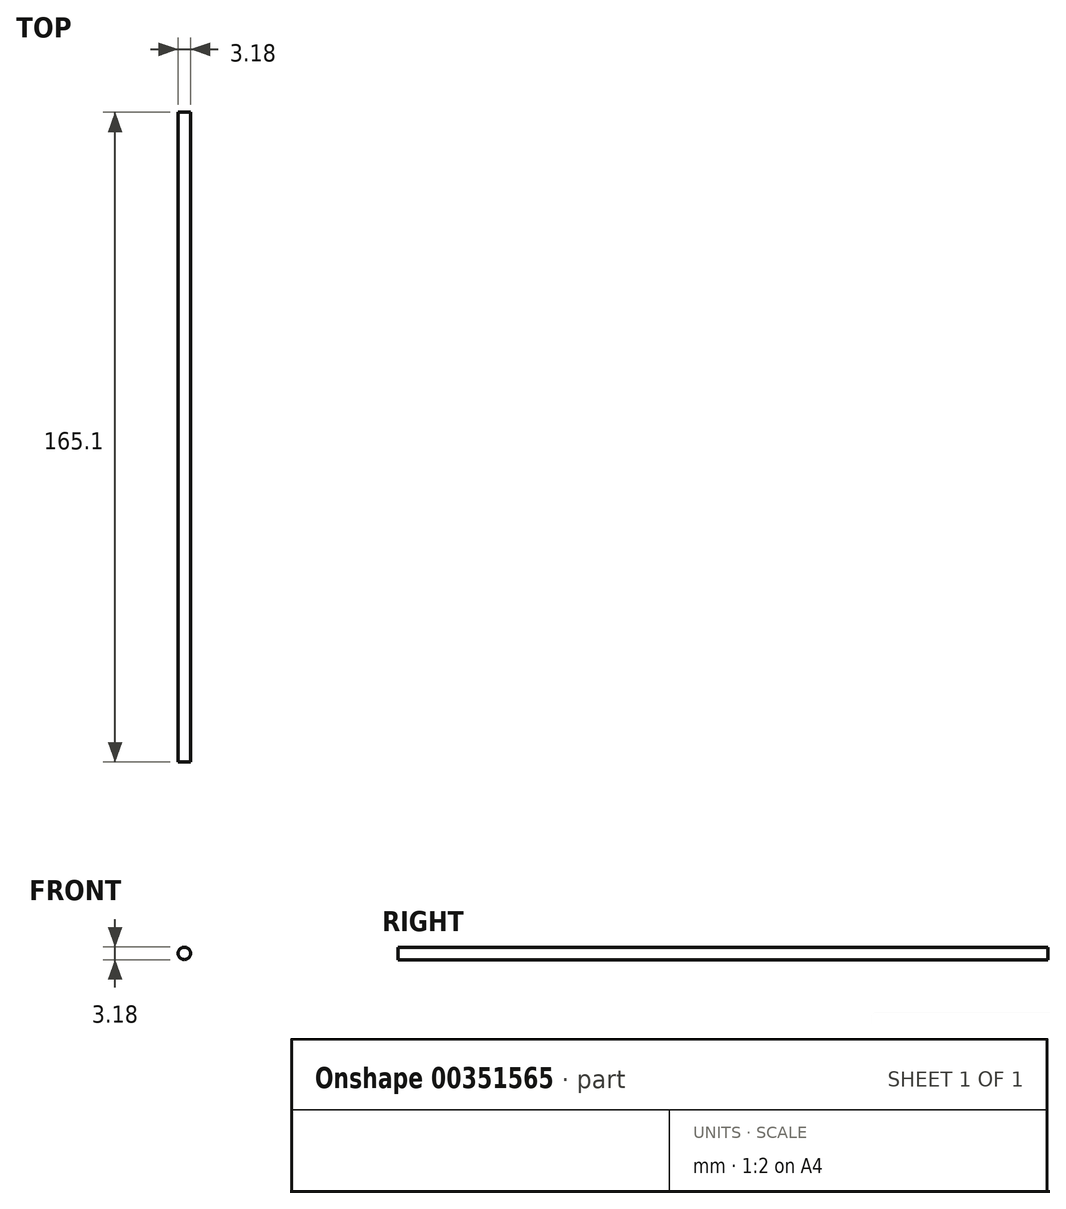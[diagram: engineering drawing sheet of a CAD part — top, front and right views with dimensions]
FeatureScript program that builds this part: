
annotation { "Feature Type Name" : "Feature", "Feature Type Description" : "" }
export const myFeature = defineFeature(function(context is Context, id is Id, definition is map)
    precondition{}
    {
        {
            var Q0;
            Q0=qCreatedBy(makeId("Front.planeOp"),FACE);
            var sketch = newSketch(context, id + "F0", { "sketchPlane" : qUnion([Q0])});
            skCircle(sketch, "E0", {"center": v(0, 0) * mm, "radius": 1.59 * mm});
            skSolve(sketch);
        }
        {
            var Q0;
            Q0=qSketchRegion(id+"F0",true);
            extrude(context, id + "F1", {"entities" : qUnion([Q0]), "depth" : 165.1 * mm, "symmetric" : true});
        }
    });
